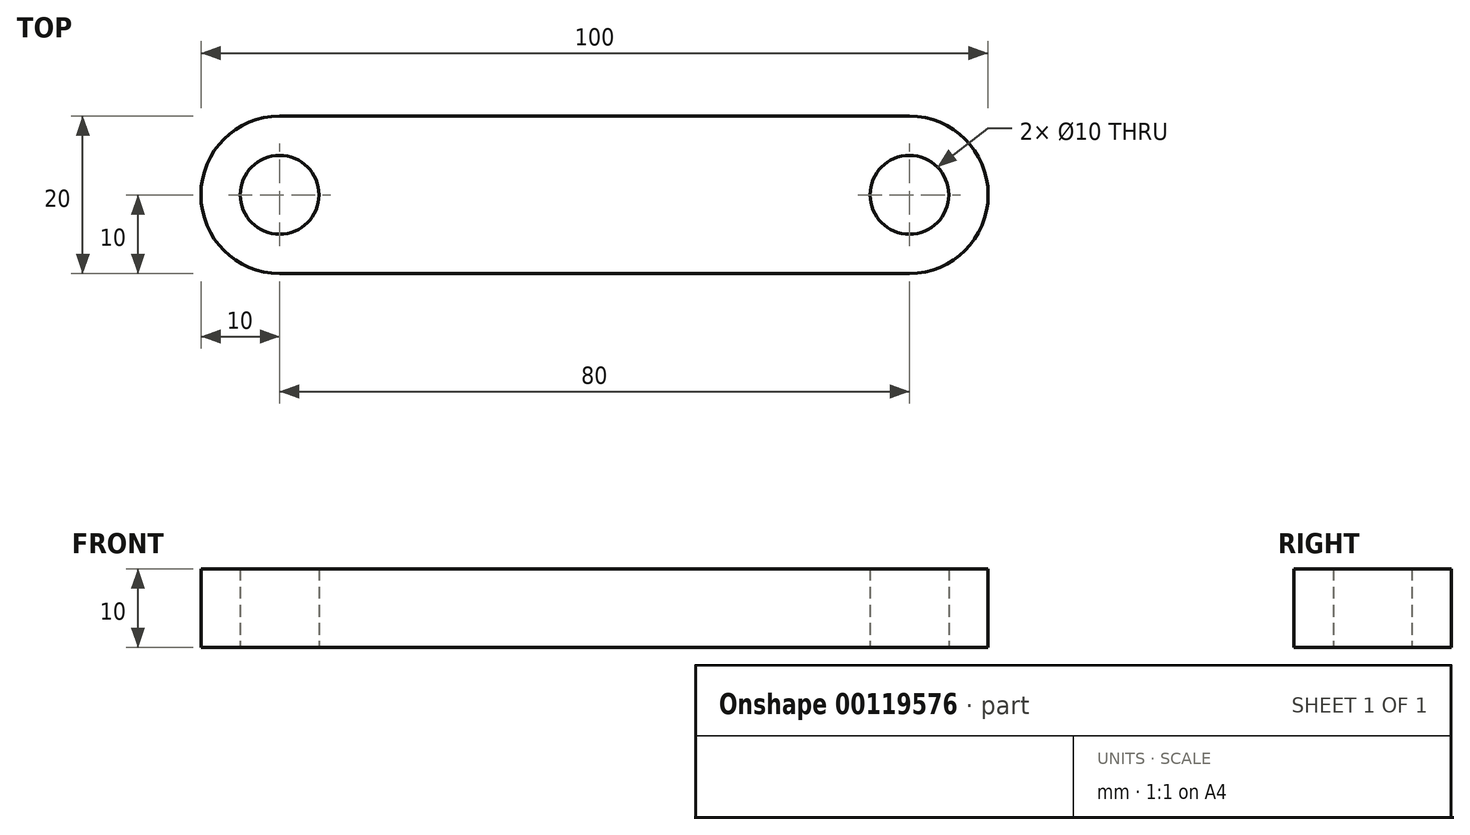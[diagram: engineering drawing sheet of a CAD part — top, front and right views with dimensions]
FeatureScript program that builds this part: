
annotation { "Feature Type Name" : "Feature", "Feature Type Description" : "" }
export const myFeature = defineFeature(function(context is Context, id is Id, definition is map)
    precondition{}
    {
        {
            var Q0;
            Q0=qCreatedBy(makeId("Top.planeOp"),FACE);
            var sketch = newSketch(context, id + "F0", { "sketchPlane" : qUnion([Q0])});
            skLineSegment(sketch, "E0.bottom", {"start": v(0, 0) * mm, "end": v(-80, 0) * mm});
            skLineSegment(sketch, "E0.top", {"start": v(0, -20) * mm, "end": v(-80, -20) * mm});
            skArc(sketch, "E1", {"start": v(-80, 0) * mm, "mid": v(-90, -10) * mm, "end": v(-80, -20) * mm});
            skArc(sketch, "E2", {"start": v(0, 0) * mm, "mid": v(10, -10) * mm, "end": v(0, -20) * mm});
            skCircle(sketch, "E3", {"center": v(-80, -10) * mm, "radius": 5 * mm});
            skCircle(sketch, "E4", {"center": v(0, -10) * mm, "radius": 5 * mm});
            skSolve(sketch);
        }
        {
            var Q0;
            Q0 = qSketchRegion(id + "F0", true);
            extrude(context, id + "F1", {"entities" : qUnion([Q0]), "depth" : 10 * mm});
        }
    });
